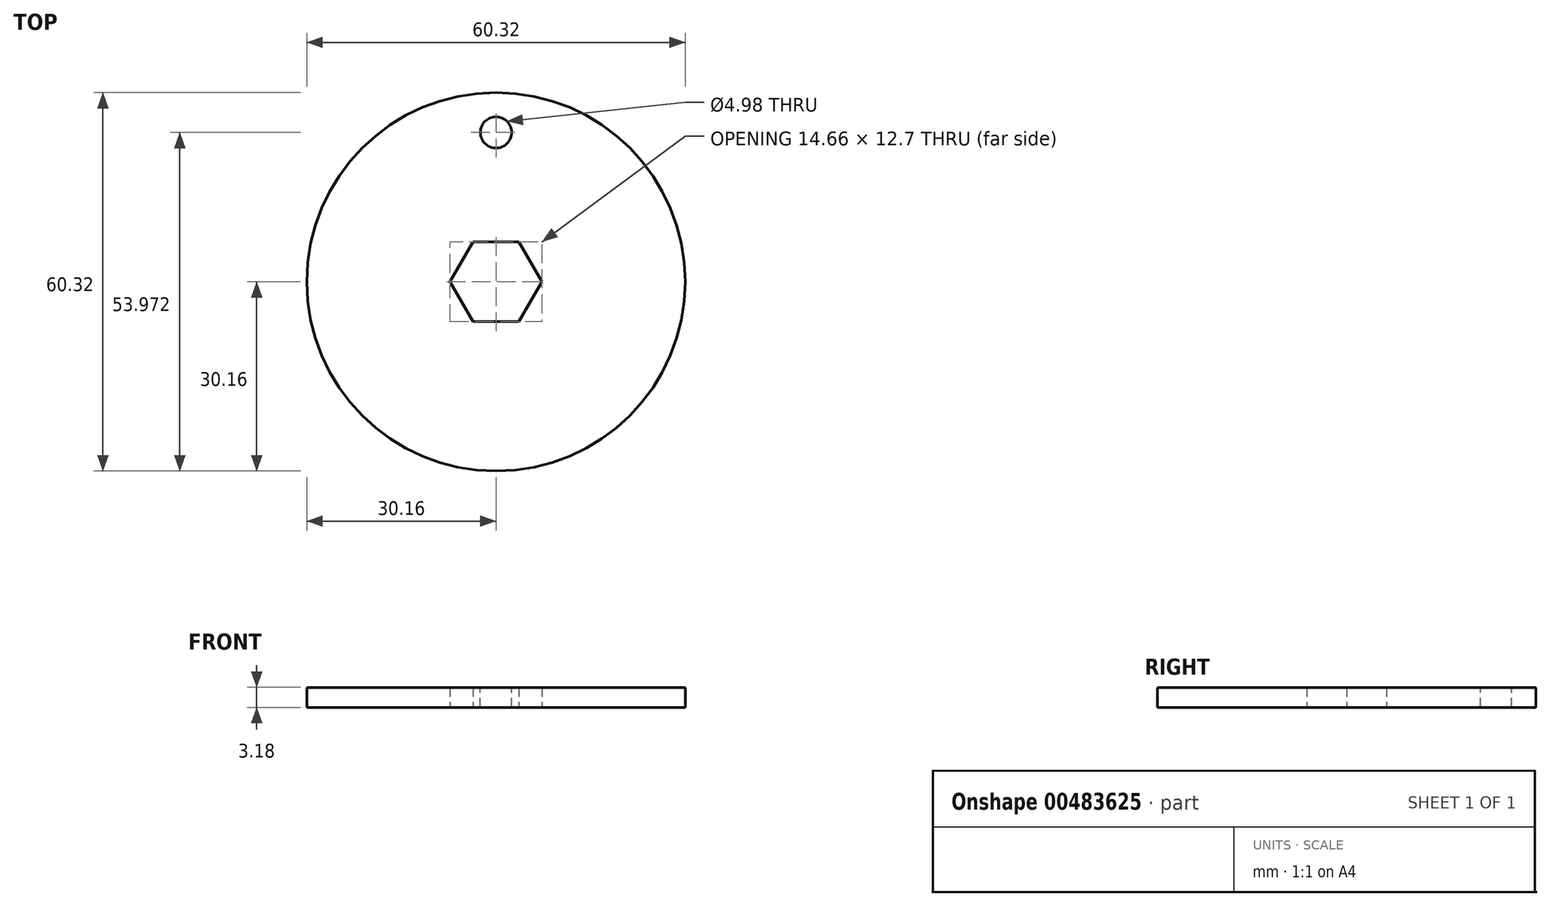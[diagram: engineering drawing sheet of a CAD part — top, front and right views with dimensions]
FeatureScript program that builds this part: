
annotation { "Feature Type Name" : "Feature", "Feature Type Description" : "" }
export const myFeature = defineFeature(function(context is Context, id is Id, definition is map)
    precondition{}
    {
        {
            var Q0;
            Q0=qCreatedBy(makeId("Top.planeOp"),FACE);
            var sketch = newSketch(context, id + "F0", { "sketchPlane" : qUnion([Q0])});
            skCircle(sketch, "E0", {"center": v(0, 0) * mm, "radius": 30.16 * mm});
            skCircle(sketch, "E1.cCircle", {"center": v(0, 0) * mm, "radius": 6.35 * mm, "construction": true});
            skLineSegment(sketch, "E1.0", {"start": v(3.67, -6.35) * mm, "end": v(-3.67, -6.35) * mm});
            skLineSegment(sketch, "E1.1", {"start": v(-3.67, -6.35) * mm, "end": v(-7.33, 0) * mm});
            skLineSegment(sketch, "E1.2", {"start": v(-7.33, 0) * mm, "end": v(-3.67, 6.35) * mm});
            skLineSegment(sketch, "E1.3", {"start": v(-3.67, 6.35) * mm, "end": v(3.67, 6.35) * mm});
            skLineSegment(sketch, "E1.4", {"start": v(3.67, 6.35) * mm, "end": v(7.33, 0) * mm});
            skLineSegment(sketch, "E1.5", {"start": v(7.33, 0) * mm, "end": v(3.67, -6.35) * mm});
            skPoint(sketch, "E1.0.midPoint", {"position": v(0, -6.35) * mm});
            skSolve(sketch);
        }
        {
            var Q0;
            Q0=makeQuery(id+"F0.imprint","IMPRINT",FACE,{"disambiguationData":[TD([[makeQuery(id+"F0.imprint","IMPRINT",EDGE,{"derivedFrom":sQuery(id+"F0.wireOp",EDGE,"E0")}),1.0]])]});
            extrude(context, id + "F1", {"entities" : qUnion([Q0]), "depth" : 3.17 * mm});
        }
        {
            var Q0;
            Q0=makeQuery(id+"F1.opExtrude","CAP_FACE",FACE,{"disambiguationData":[OSD([sQuery(id+"F0.wireOp",EDGE,"E0"),sQuery(id+"F0.wireOp",EDGE,"GgrIKYkA-Vwx4-oePL-x3LN-7GwLvUZ36auW")])],"isStart":false});
            var sketch = newSketch(context, id + "F2", { "sketchPlane" : qUnion([Q0])});
            skCircle(sketch, "E2", {"center": v(0, 23.81) * mm, "radius": 2.49 * mm});
            skCircle(sketch, "E3", {"center": v(0, 76.2) * mm, "radius": 2.49 * mm, "construction": true});
            skCircle(sketch, "E4", {"center": v(25.4, 44) * mm, "radius": 2.49 * mm, "construction": true});
            skLineSegment(sketch, "E5", {"start": v(0, 0) * mm, "end": v(25.4, 44) * mm, "construction": true});
            skSolve(sketch);
        }
        {
            var Q0;
            Q0=qSketchRegion(id+"F2",true);
            extrude(context, id + "F3", {"entities" : qUnion([Q0]), "operationType" : NewBodyOperationType.REMOVE, "endBound" : BoundingType.THROUGH_ALL, "oppositeDirection" : true, "depth" : 25.4 * mm});
        }
        {
            var Q0;
            Q0=makeQuery(id+"F1.opExtrude","CAP_FACE",FACE,{"disambiguationData":[OSD([sQuery(id+"F0.wireOp",EDGE,"E0"),sQuery(id+"F0.wireOp",EDGE,"GgrIKYkA-Vwx4-oePL-x3LN-7GwLvUZ36auW")])],"isStart":false});
            var sketch = newSketch(context, id + "F4", { "sketchPlane" : qUnion([Q0])});
            skCircle(sketch, "E6.cCircle", {"center": v(0, 0) * mm, "radius": 32.58 * mm, "construction": true});
            skLineSegment(sketch, "E6.0", {"start": v(23.67, -32.58) * mm, "end": v(-23.67, -32.58) * mm, "construction": true});
            skLineSegment(sketch, "E6.1", {"start": v(-23.67, -32.58) * mm, "end": v(-38.3, 12.45) * mm, "construction": true});
            skLineSegment(sketch, "E6.2", {"start": v(-38.3, 12.45) * mm, "end": v(0, 40.27) * mm, "construction": true});
            skLineSegment(sketch, "E6.3", {"start": v(0, 40.27) * mm, "end": v(38.3, 12.45) * mm, "construction": true});
            skLineSegment(sketch, "E6.4", {"start": v(38.3, 12.45) * mm, "end": v(23.67, -32.58) * mm, "construction": true});
            skPoint(sketch, "E6.0.midPoint", {"position": v(0, -32.58) * mm});
            skCircle(sketch, "E7", {"center": v(0, 40.27) * mm, "radius": 2.36 * mm});
            skCircle(sketch, "E8", {"center": v(38.3, 12.45) * mm, "radius": 2.36 * mm});
            skCircle(sketch, "E9", {"center": v(23.67, -32.58) * mm, "radius": 2.36 * mm});
            skCircle(sketch, "E10", {"center": v(-23.67, -32.58) * mm, "radius": 2.36 * mm});
            skCircle(sketch, "E11", {"center": v(-38.3, 12.45) * mm, "radius": 2.36 * mm});
            skCircle(sketch, "E12", {"center": v(0, 0) * mm, "radius": 40.27 * mm, "construction": true});
            skSolve(sketch);
        }
        {
            var Q0;
            Q0=qSketchRegion(id+"F4",true);
            extrude(context, id + "F5", {"entities" : qUnion([Q0]), "operationType" : NewBodyOperationType.REMOVE, "endBound" : BoundingType.THROUGH_ALL, "oppositeDirection" : true, "depth" : 25.4 * mm});
        }
    });
